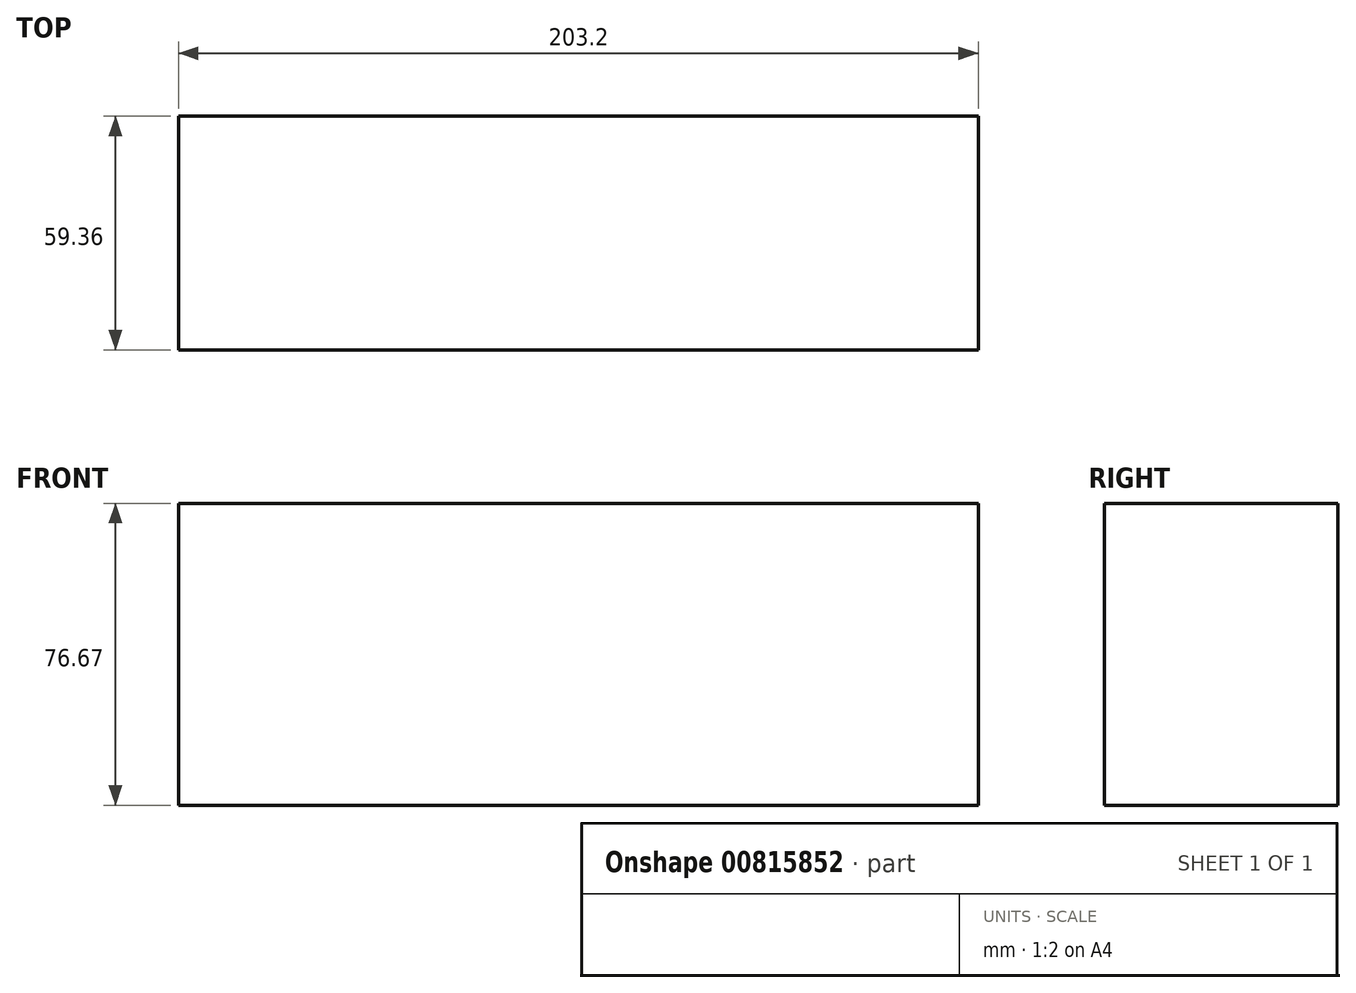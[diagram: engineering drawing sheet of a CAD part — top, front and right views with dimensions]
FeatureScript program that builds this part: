
annotation { "Feature Type Name" : "Feature", "Feature Type Description" : "" }
export const myFeature = defineFeature(function(context is Context, id is Id, definition is map)
    precondition{}
    {
        {
            var Q0;
            Q0=qCreatedBy(makeId("Right.planeOp"),FACE);
            var sketch = newSketch(context, id + "F0", { "sketchPlane" : qUnion([Q0])});
            skLineSegment(sketch, "E0.bottom", {"start": v(-30.1, 0) * mm, "end": v(29.08, 0) * mm});
            skLineSegment(sketch, "E0.top", {"start": v(-30.1, -8.38) * mm, "end": v(29.08, -8.38) * mm});
            skLineSegment(sketch, "E0.left", {"start": v(-30.1, 0) * mm, "end": v(-30.1, -8.38) * mm});
            skLineSegment(sketch, "E0.right", {"start": v(29.08, 0) * mm, "end": v(29.08, -8.38) * mm});
            skLineSegment(sketch, "E1.bottom", {"start": v(-30.1, 0) * mm, "end": v(29.26, 0) * mm});
            skLineSegment(sketch, "E1.top", {"start": v(-30.1, 76.67) * mm, "end": v(29.26, 76.67) * mm});
            skLineSegment(sketch, "E1.left", {"start": v(-30.1, 0) * mm, "end": v(-30.1, 76.67) * mm});
            skLineSegment(sketch, "E1.right", {"start": v(29.26, 0) * mm, "end": v(29.26, 76.67) * mm});
            skLineSegment(sketch, "E2.bottom", {"start": v(-30.1, 76.67) * mm, "end": v(49.82, 76.67) * mm});
            skLineSegment(sketch, "E2.top", {"start": v(-30.1, 93.44) * mm, "end": v(49.82, 93.44) * mm});
            skLineSegment(sketch, "E2.left", {"start": v(-30.1, 76.67) * mm, "end": v(-30.1, 93.44) * mm});
            skLineSegment(sketch, "E2.right", {"start": v(49.82, 76.67) * mm, "end": v(49.82, 93.44) * mm});
            skLineSegment(sketch, "E3.bottom", {"start": v(-20.48, 93.44) * mm, "end": v(29.48, 93.44) * mm});
            skLineSegment(sketch, "E3.top", {"start": v(-20.48, 131.54) * mm, "end": v(29.48, 131.54) * mm});
            skLineSegment(sketch, "E3.left", {"start": v(-20.48, 93.44) * mm, "end": v(-20.48, 131.54) * mm});
            skLineSegment(sketch, "E3.right", {"start": v(29.48, 93.44) * mm, "end": v(29.48, 131.54) * mm});
            skLineSegment(sketch, "E4.bottom", {"start": v(-20.48, 131.54) * mm, "end": v(29.67, 131.54) * mm});
            skLineSegment(sketch, "E4.top", {"start": v(-20.48, 138.63) * mm, "end": v(29.67, 138.63) * mm});
            skLineSegment(sketch, "E4.left", {"start": v(-20.48, 131.54) * mm, "end": v(-20.48, 138.63) * mm});
            skLineSegment(sketch, "E4.right", {"start": v(29.67, 131.54) * mm, "end": v(29.67, 138.63) * mm});
            skLineSegment(sketch, "E5.bottom", {"start": v(-8.68, 138.63) * mm, "end": v(20.59, 138.63) * mm});
            skLineSegment(sketch, "E5.top", {"start": v(-8.68, 184.05) * mm, "end": v(20.59, 184.05) * mm});
            skLineSegment(sketch, "E5.left", {"start": v(-8.68, 138.63) * mm, "end": v(-8.68, 184.05) * mm});
            skLineSegment(sketch, "E5.right", {"start": v(20.59, 138.63) * mm, "end": v(20.59, 184.05) * mm});
            skSolve(sketch);
        }
        {
            var Q0;
            {var subQ1=sQuery(id+"F0.wireOp",EDGE,"E1.left");Q0=makeQuery(id+"F0.imprint","IMPRINT",FACE,{"disambiguationData":[TD([[makeQuery(id+"F0.imprint","IMPRINT",EDGE,{"derivedFrom":subQ1}),-1.0]])]});}
            extrude(context, id + "F1", {"entities" : qUnion([Q0]), "oppositeDirection" : true, "depth" : 203.2 * mm, "offsetDistance" : 25.4 * mm});
        }
    });
